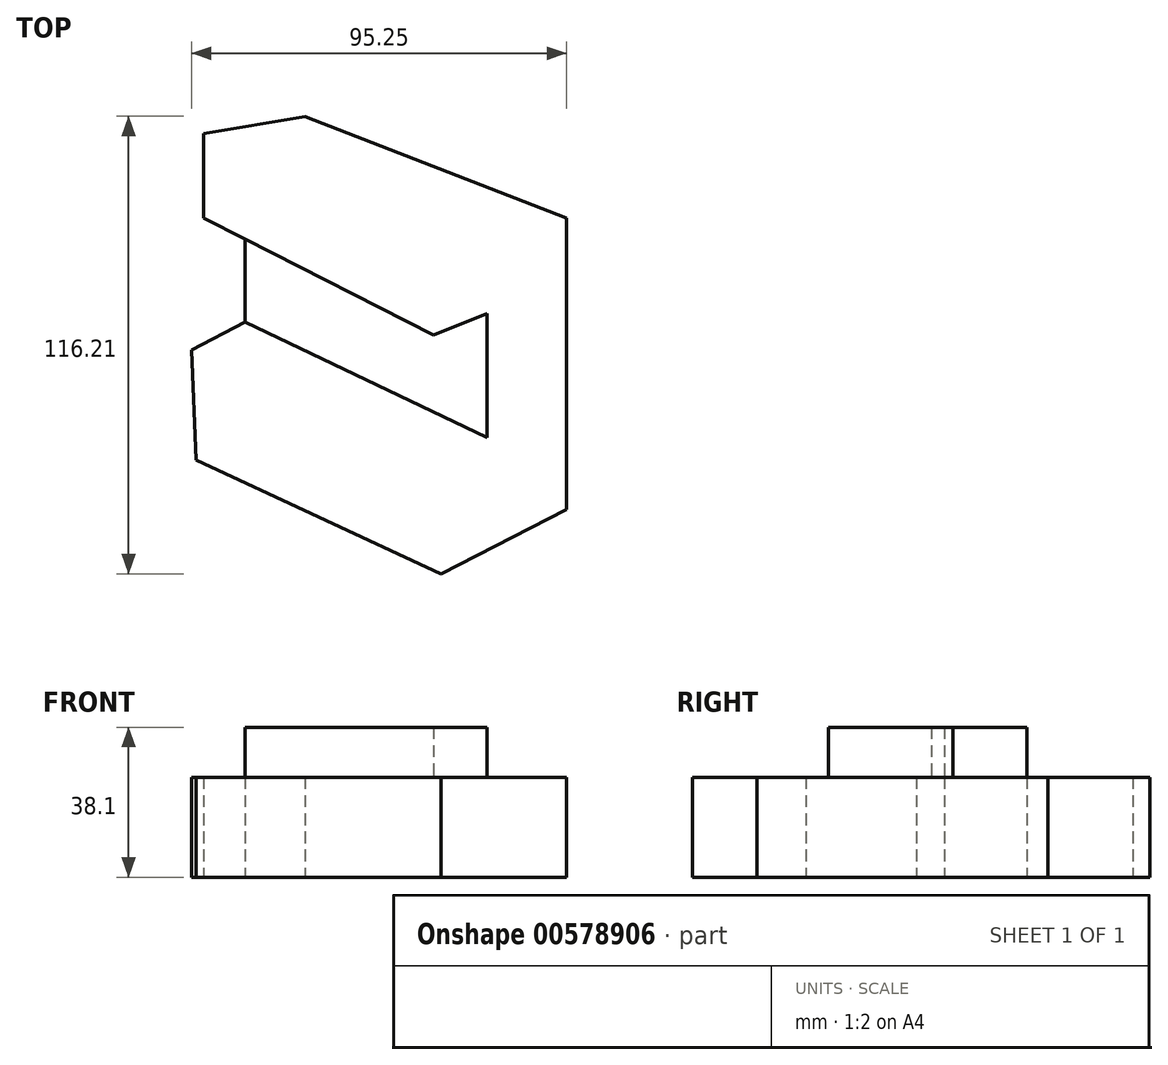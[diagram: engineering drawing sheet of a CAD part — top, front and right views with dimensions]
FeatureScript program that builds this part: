
annotation { "Feature Type Name" : "Feature", "Feature Type Description" : "" }
export const myFeature = defineFeature(function(context is Context, id is Id, definition is map)
    precondition{}
    {
        {
            var Q0;
            Q0=qCreatedBy(makeId("Top.planeOp"),FACE);
            var sketch = newSketch(context, id + "F0", { "sketchPlane" : qUnion([Q0])});
            skLineSegment(sketch, "E0", {"start": v(-47.63, 54.97) * mm, "end": v(10.61, 25.3) * mm});
            skLineSegment(sketch, "E1", {"start": v(-47.63, 54.97) * mm, "end": v(-47.63, 33.47) * mm});
            skLineSegment(sketch, "E2", {"start": v(10.61, 25.3) * mm, "end": v(10.61, 4.08) * mm});
            skLineSegment(sketch, "E3", {"start": v(-47.63, 33.47) * mm, "end": v(10.61, 4.08) * mm});
            skLineSegment(sketch, "E4", {"start": v(10.61, 4.08) * mm, "end": v(24.76, 9.8) * mm});
            skLineSegment(sketch, "E5", {"start": v(24.76, 9.8) * mm, "end": v(24.76, -22.59) * mm});
            skLineSegment(sketch, "E6", {"start": v(24.76, -22.59) * mm, "end": v(12.8, -27.76) * mm});
            skLineSegment(sketch, "E7", {"start": v(12.8, -27.76) * mm, "end": v(12.8, -56.88) * mm});
            skLineSegment(sketch, "E8", {"start": v(12.8, -56.88) * mm, "end": v(44.63, -40.55) * mm});
            skLineSegment(sketch, "E9", {"start": v(44.63, -40.55) * mm, "end": v(44.63, 33.47) * mm});
            skLineSegment(sketch, "E10", {"start": v(10.61, 25.3) * mm, "end": v(44.63, 33.47) * mm});
            skLineSegment(sketch, "E11", {"start": v(44.63, 33.47) * mm, "end": v(-21.77, 59.33) * mm});
            skLineSegment(sketch, "E12", {"start": v(-47.63, 54.97) * mm, "end": v(-21.77, 59.33) * mm});
            skLineSegment(sketch, "E13", {"start": v(24.76, -22.59) * mm, "end": v(-37.01, 7.08) * mm});
            skLineSegment(sketch, "E14", {"start": v(-37.01, 7.08) * mm, "end": v(-37.01, 28.12) * mm});
            skLineSegment(sketch, "E15", {"start": v(-37.01, 7.08) * mm, "end": v(-50.62, 0) * mm});
            skLineSegment(sketch, "E16", {"start": v(-50.62, 0) * mm, "end": v(12.8, -27.76) * mm});
            skLineSegment(sketch, "E17", {"start": v(12.8, -56.88) * mm, "end": v(-49.53, -28.03) * mm});
            skLineSegment(sketch, "E18", {"start": v(-50.62, 0) * mm, "end": v(-49.53, -28.03) * mm});
            skSolve(sketch);
        }
        {
            var Q0;
            Q0 = qSketchRegion(id + "F0", true);
            extrude(context, id + "F1", {"entities" : qUnion([Q0]), "depth" : 25.4 * mm, "offsetDistance" : 25.4 * mm});
        }
        {
            var Q0;
            Q0=makeQuery(id+"F1.opExtrude","CAP_FACE",FACE,{"disambiguationData":[OSD([sQuery(id+"F0.wireOp",EDGE,"E1"),sQuery(id+"F0.wireOp",EDGE,"E3"),sQuery(id+"F0.wireOp",EDGE,"E8"),sQuery(id+"F0.wireOp",EDGE,"E9"),sQuery(id+"F0.wireOp",EDGE,"E11"),sQuery(id+"F0.wireOp",EDGE,"E12"),sQuery(id+"F0.wireOp",EDGE,"E14"),sQuery(id+"F0.wireOp",EDGE,"E15"),sQuery(id+"F0.wireOp",EDGE,"E17"),sQuery(id+"F0.wireOp",EDGE,"E18")])],"isStart":false});
            var sketch = newSketch(context, id + "F2", { "sketchPlane" : qUnion([Q0])});
            skLineSegment(sketch, "E19", {"start": v(-37.01, 28.12) * mm, "end": v(10.89, 3.81) * mm});
            skLineSegment(sketch, "E20", {"start": v(10.89, 3.81) * mm, "end": v(24.5, 9.25) * mm});
            skLineSegment(sketch, "E21", {"start": v(24.5, 9.25) * mm, "end": v(24.5, -22.32) * mm});
            skLineSegment(sketch, "E22", {"start": v(-37.01, 7.08) * mm, "end": v(24.5, -22.32) * mm});
            skLineSegment(sketch, "E23", {"start": v(-37.01, 28.12) * mm, "end": v(-37.01, 7.08) * mm});
            skSolve(sketch);
        }
        {
            var Q0;
            Q0=makeQuery(id+"F2.imprint","IMPRINT",FACE,{"disambiguationData":[TD([[makeQuery(id+"F2.imprint","IMPRINT",EDGE,{"derivedFrom":sQuery(id+"F2.wireOp",EDGE,"E19")}),-1.0]])]});
            extrude(context, id + "F3", {"entities" : qUnion([Q0]), "operationType" : NewBodyOperationType.ADD, "depth" : 12.7 * mm, "offsetDistance" : 25.4 * mm});
        }
    });
